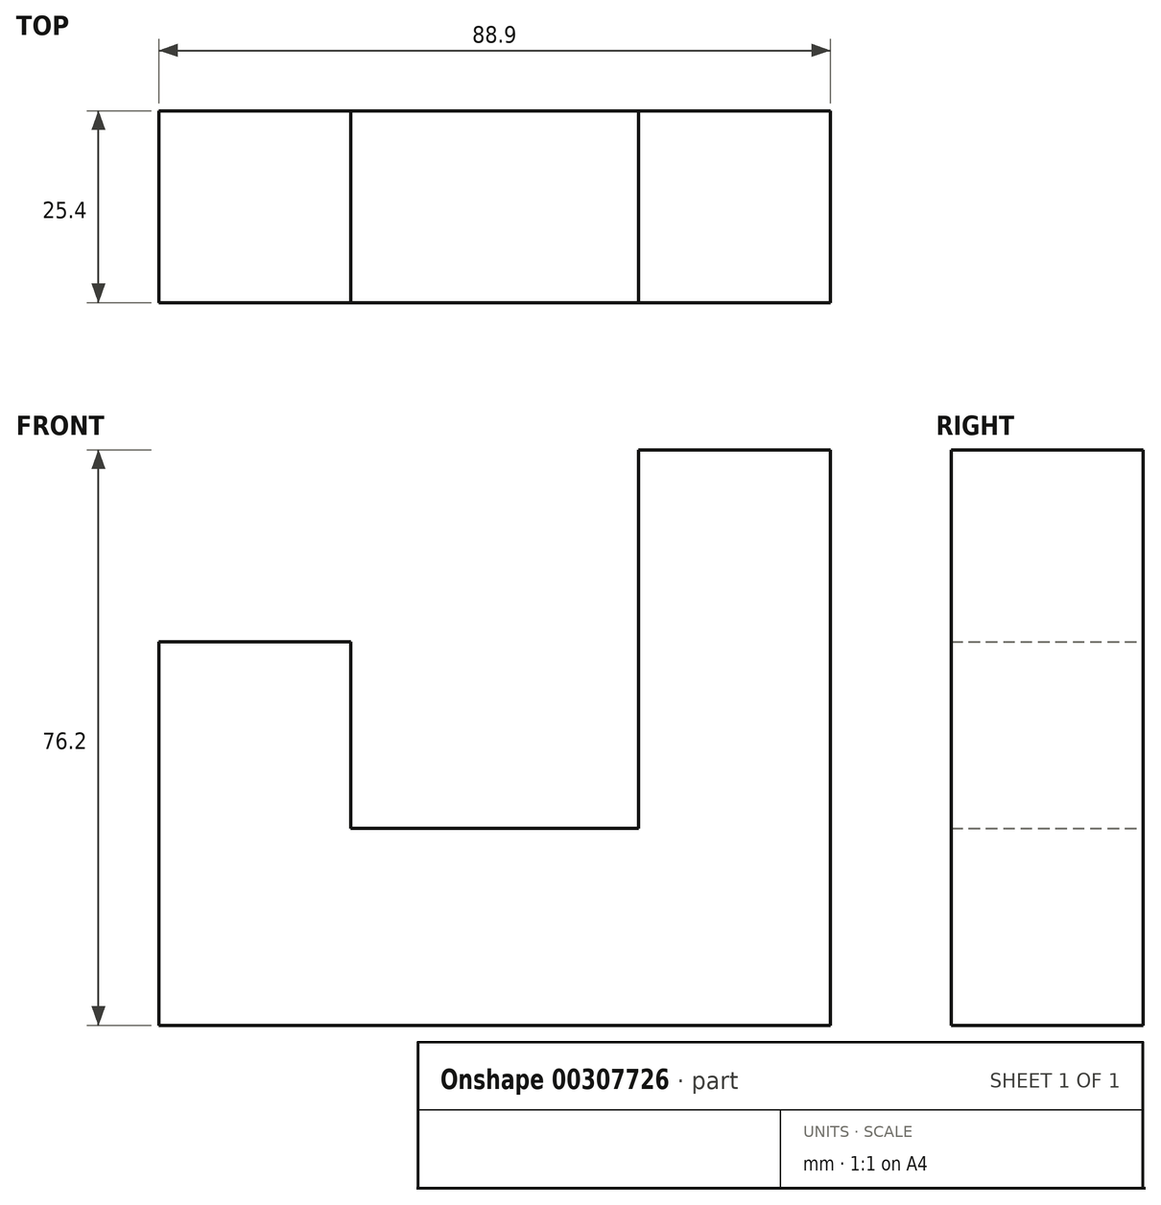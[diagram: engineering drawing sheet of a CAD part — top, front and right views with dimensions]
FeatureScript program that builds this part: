
annotation { "Feature Type Name" : "Feature", "Feature Type Description" : "" }
export const myFeature = defineFeature(function(context is Context, id is Id, definition is map)
    precondition{}
    {
        {
            var Q0;
            Q0=qCreatedBy(makeId("Front.planeOp"),FACE);
            var sketch = newSketch(context, id + "F0", { "sketchPlane" : qUnion([Q0])});
            skLineSegment(sketch, "E0", {"start": v(-51.01, -47.2) * mm, "end": v(37.89, -47.2) * mm});
            skLineSegment(sketch, "E1", {"start": v(37.89, -47.2) * mm, "end": v(37.89, 29) * mm});
            skLineSegment(sketch, "E2", {"start": v(37.89, 29) * mm, "end": v(12.49, 29) * mm});
            skLineSegment(sketch, "E3", {"start": v(12.49, 29) * mm, "end": v(12.49, -21.15) * mm});
            skLineSegment(sketch, "E4", {"start": v(12.49, -21.15) * mm, "end": v(-25.61, -21.15) * mm});
            skLineSegment(sketch, "E5", {"start": v(-25.61, -21.15) * mm, "end": v(-25.61, 3.6) * mm});
            skLineSegment(sketch, "E6", {"start": v(-25.61, 3.6) * mm, "end": v(-51.01, 3.6) * mm});
            skLineSegment(sketch, "E7", {"start": v(-51.01, 3.6) * mm, "end": v(-51.01, -47.2) * mm});
            skSolve(sketch);
        }
        {
            var Q0;
            Q0=makeQuery(id+"F0.imprint","IMPRINT",FACE,{"disambiguationData":[TD([[makeQuery(id+"F0.imprint","IMPRINT",EDGE,{"derivedFrom":sQuery(id+"F0.wireOp",EDGE,"E0")}),1.0]])]});
            extrude(context, id + "F1", {"entities" : qUnion([Q0]), "depth" : 25.4 * mm});
        }
    });
